# Revit family: Domotics-DomesticRanges-GEWISS-SYSTEM_POWER-SOCKET-OUTLET_ITADEU_P17P30_16A
name_source: partatom
category: Apparecchi elettrici
revit_build: Autodesk Revit 2016 (Build: 20161004_0715(x64)
units: mm (PartAtom-declared; Revit-internal decimal feet)

## family parameters
Condiviso = Sì
Host = Superficie
Mantenere orientamento annotazione = Sì
Numero OmniClass = 23.80.50.14
Punto di calcolo locali = Sì
Quota connettore circolare = Usa diametro
Taglio con vuoti quando caricato = No
Tipo di parte = Normale
Titolo OmniClass = Plug Connectors

## types (5) — shared parameters
Catalogue = DOMOTICS
Catalogue Range = SYSTEM - DOMESTIC RANGE
Characteristics = 2P+E - 16 A Dual amperage
Description. = Dual amperage socket-outlet
Description: = 2P+E - 16 A Dual amperage
Earth pit = Side and central
Electrocod = 0131
For plug pins = Ã˜ 4 / 4.8 / 5 mm
IDF = f3cd7a5d-e64c-49b7-bd89-3a58705ebebc
IDT = 73571261-b7db-4f3e-b3f6-90da01f7c4b0
Immagine tipo = <Nessuno>
Larghezza presa = 46 mm  [stored 0.150919 ft]
No. SYSTEM modules = 2
Produttore = GEWISS S.p.A.
Prospetto di default = 1219 mm
Pulsasnte = GEWISS NERO
SEO = Socket outlet
Simbolo = SIMBOLO PRESE : PRESA
Standard = Italian / German
Standard: = Italian / German
Technical sheet = https://www.gewiss.com
Tipo_ = SYSTEM PRESE ITAGER P17-30 16A_BASE : GW20246 - PRESA 2P+T 16A BIV.ST.ITALIANO/TED.SY/WT
Type = P40
Typology = P30 - P17
URL = https://www.gewiss.com
Version file RFA = 19.4
Voltage = 250 V ac
Voltage: = 250 V ac

## per-type parameters (varying)
| type | Colour | Descrizione | EAN code | Modello | Type: |
| GW21246 - 16A 2P+E d.a. Ital./ger s.-out. black | Black | 16A 2P+E D.A. ITAL./GER S.-OUT. SY/BLACK | 8011564128422 | GW21246 |  |
| GW20287 - 2P+E 16A d.amp ita/ger st.orange sock. | Orange | 2P+E 16A D.AMP ITA/GER ST.ORANGE SOCK. | 8011564079465 | GW20287 | For allocated lines |
| GW20246 - 16A 2P+E d.a. Ital./ger s.-out. white | White | 16A 2P+E D.A. ITAL./GER S.-OUT. SY/WT | 8011564025974 | GW20246 |  |
| GW20282 - 2P+E 16A d.amp ita/ger st.green sock. | Green | 2P+E 16A D.AMP ITA/GER ST.GREEN SOCK. | 8011564079434 | GW20282 | For allocated lines |
| GW20296 - 2P+E 16A d.amp ita/ger st.red sock. | Red | 2P+E 16A D.AMP ITA/GER ST.RED SOCK. | 8011564044876 | GW20296 | For allocated lines |

note: [stored X ft] marks values corroborated as IEEE doubles in the binary element streams (Revit-internal decimal feet)

## geometry (parser evidence)
native form markers: Sweep x2
no freeform markers — native parametric forms only
